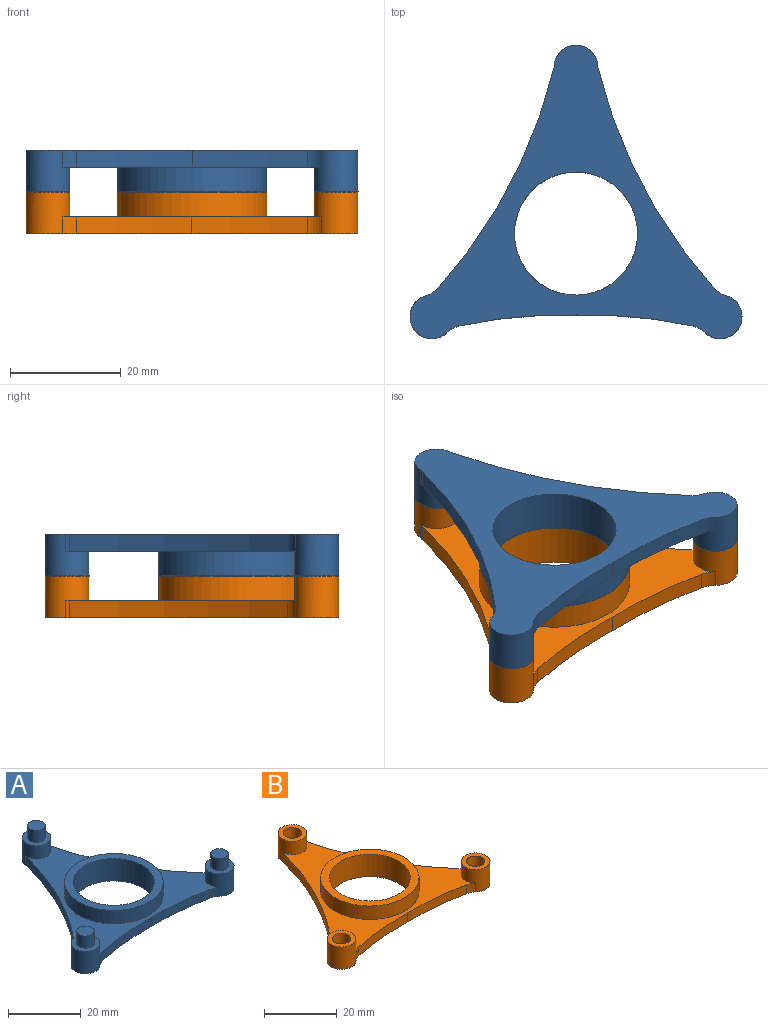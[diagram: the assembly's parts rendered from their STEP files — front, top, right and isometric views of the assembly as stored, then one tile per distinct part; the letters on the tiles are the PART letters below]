
ASSEMBLY  parts=2 mates=1
PART A: 27 faces, bbox 59.9x52.9x11.5 mm
  f0: cylinder r=92.19mm len=39.27mm, axis (0,0,-1), area 134.5mm2, adj f4,f5,f15,f16
  f1: cylinder r=92.19mm len=20.84mm, axis (0,0,-1), area 62.9mm2, adj f2,f4,f5,f17
  f2: cylinder r=92.19mm len=20.84mm, axis (0,0,-1), area 62.9mm2, adj f1,f4,f5,f18
  f3: cylinder r=92.19mm len=39.27mm, axis (0,0,-1), area 134.5mm2, adj f4,f5,f19,f20
  f4: plane 54.21x48.19mm, normal (0,0,1), area 641.9mm2, adj f0,f1,f2,f3,f6,f8,f10,f12
  f5: plane 59.86x52.9mm, normal (0,0,-1), area 974.4mm2, adj f0,f1,f2,f3,f6,f8,f10,f13
  f6: cylinder r=3.95mm len=7.9mm, axis (0,0,-1), area 147mm2, adj f4,f5,f7,f15,f20
  f7: plane 7.9x7.9mm, normal (0,0,1), area 30.9mm2, adj f6,f25
  f8: cylinder r=3.95mm len=7.9mm, axis (0,0,-1), area 154.5mm2, adj f4,f5,f9,f16,f17
  f9: plane 7.9x7.9mm, normal (0,0,1), area 30.9mm2, adj f8,f21
  f10: cylinder r=3.95mm len=7.9mm, axis (0,0,-1), area 154.5mm2, adj f4,f5,f11,f18,f19
  f11: plane 7.9x7.9mm, normal (0,0,1), area 30.9mm2, adj f10,f23
  f12: cylinder r=13.5mm len=27mm, axis (0,0,-1), area 381.7mm2, adj f4,f14
  f13: cylinder r=11.1mm len=22.2mm, axis (0,0,-1), area 523.1mm2, adj f5,f14
  f14: plane 27x27mm, normal (0,0,1), area 185.5mm2, adj f12,f13
  f15: cylinder r=5mm len=3mm, axis (0,0,-1), area 2.4mm2, adj f0,f4,f5,f6
  f16: cylinder r=5mm len=3mm, axis (0,0,-1), area 8.3mm2, adj f0,f4,f5,f8
  f17: cylinder r=5mm len=3mm, axis (0,0,-1), area 8.3mm2, adj f1,f4,f5,f8
  f18: cylinder r=5mm len=3mm, axis (0,0,-1), area 8.3mm2, adj f2,f4,f5,f10
  f19: cylinder r=5mm len=3mm, axis (0,0,-1), area 8.3mm2, adj f3,f4,f5,f10
  f20: cylinder r=5mm len=3mm, axis (0,0,-1), area 2.4mm2, adj f3,f4,f5,f6
  f21: cylinder r=2.4mm len=4.8mm, axis (0,0,-1), area 60.3mm2, adj f9,f22
  f22: plane 4.8x4.8mm, normal (0,0,1), area 18.1mm2, adj f21
  f23: cylinder r=2.4mm len=4.8mm, axis (0,0,-1), area 60.3mm2, adj f11,f24
  f24: plane 4.8x4.8mm, normal (0,0,1), area 18.1mm2, adj f23
  f25: cylinder r=2.4mm len=4.8mm, axis (0,0,-1), area 60.3mm2, adj f7,f26
  f26: plane 4.8x4.8mm, normal (0,0,1), area 18.1mm2, adj f25
PART B: 27 faces, bbox 59.9x52.9x7.5 mm
  f0: cylinder r=92.19mm len=39.27mm, axis (0,0,-1), area 134.5mm2, adj f4,f5,f15,f16
  f1: cylinder r=92.19mm len=20.84mm, axis (0,0,-1), area 62.9mm2, adj f2,f4,f5,f17
  f2: cylinder r=92.19mm len=20.84mm, axis (0,0,-1), area 62.9mm2, adj f1,f4,f5,f18
  f3: cylinder r=92.19mm len=39.27mm, axis (0,0,-1), area 134.5mm2, adj f4,f5,f19,f20
  f4: plane 54.21x48.19mm, normal (0,0,1), area 641.9mm2, adj f0,f1,f2,f3,f6,f8,f10,f12
  f5: plane 59.86x52.9mm, normal (0,0,-1), area 974.4mm2, adj f0,f1,f2,f3,f6,f8,f10,f13
  f6: cylinder r=3.95mm len=7.9mm, axis (0,0,-1), area 147mm2, adj f4,f5,f7,f15,f20
  f7: plane 7.9x7.9mm, normal (0,0,1), area 29.4mm2, adj f6,f25
  f8: cylinder r=3.95mm len=7.9mm, axis (0,0,-1), area 154.5mm2, adj f4,f5,f9,f16,f17
  f9: plane 7.9x7.9mm, normal (0,0,1), area 29.4mm2, adj f8,f23
  f10: cylinder r=3.95mm len=7.9mm, axis (0,0,-1), area 154.5mm2, adj f4,f5,f11,f18,f19
  f11: plane 7.9x7.9mm, normal (0,0,1), area 29.4mm2, adj f10,f21
  f12: cylinder r=13.5mm len=27mm, axis (0,0,-1), area 381.7mm2, adj f4,f14
  f13: cylinder r=11.1mm len=22.2mm, axis (0,0,-1), area 523.1mm2, adj f5,f14
  f14: plane 27x27mm, normal (0,0,1), area 185.5mm2, adj f12,f13
  f15: cylinder r=5mm len=3mm, axis (0,0,-1), area 2.4mm2, adj f0,f4,f5,f6
  f16: cylinder r=5mm len=3mm, axis (0,0,-1), area 8.3mm2, adj f0,f4,f5,f8
  f17: cylinder r=5mm len=3mm, axis (0,0,-1), area 8.3mm2, adj f1,f4,f5,f8
  f18: cylinder r=5mm len=3mm, axis (0,0,-1), area 8.3mm2, adj f2,f4,f5,f10
  f19: cylinder r=5mm len=3mm, axis (0,0,-1), area 8.3mm2, adj f3,f4,f5,f10
  f20: cylinder r=5mm len=3mm, axis (0,0,-1), area 2.4mm2, adj f3,f4,f5,f6
  f21: cylinder r=2.5mm len=5mm, axis (0,0,1), area 62.8mm2, adj f11,f22
  f22: plane 5x5mm, normal (0,0,1), area 19.6mm2, adj f21
  f23: cylinder r=2.5mm len=5mm, axis (0,0,1), area 62.8mm2, adj f9,f24
  f24: plane 5x5mm, normal (0,0,1), area 19.6mm2, adj f23
  f25: cylinder r=2.5mm len=5mm, axis (0,0,1), area 62.8mm2, adj f7,f26
  f26: plane 5x5mm, normal (0,0,1), area 19.6mm2, adj f25
PLACE A rot(axis=(0,-1,0),180deg) t=(-62.12,22.88,32.75)mm
PLACE B t=(-62.12,22.88,17.75)mm
MATE fastened B.f10 <-> A.f8  axis (0,0,1) through (-36.14,7.88,23.25)mm
